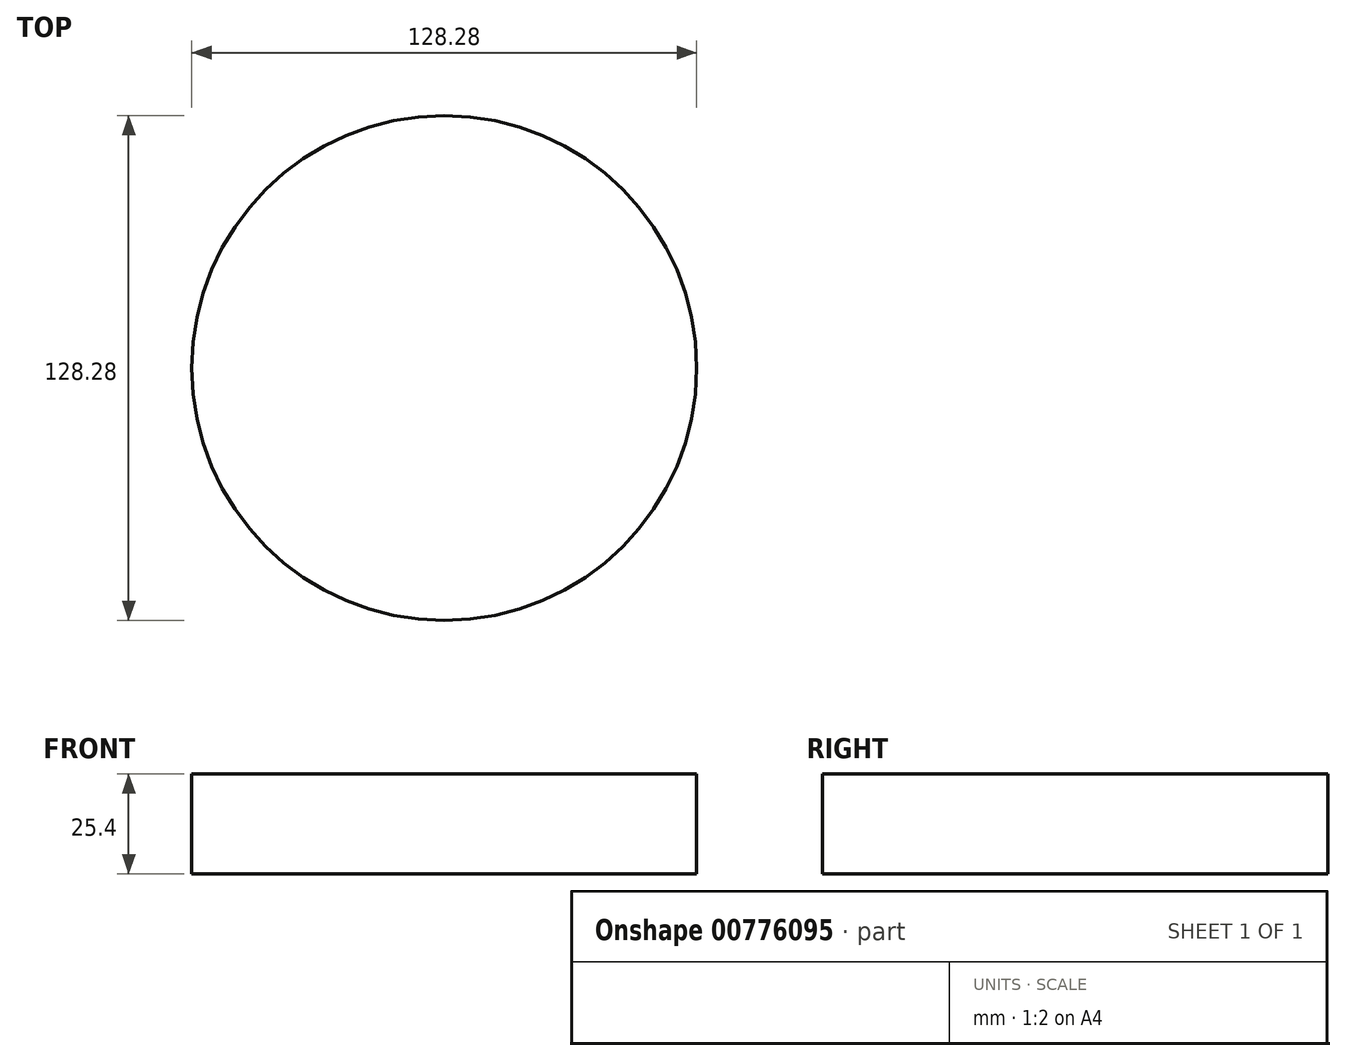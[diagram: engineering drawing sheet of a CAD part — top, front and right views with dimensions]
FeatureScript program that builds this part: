
annotation { "Feature Type Name" : "Feature", "Feature Type Description" : "" }
export const myFeature = defineFeature(function(context is Context, id is Id, definition is map)
    precondition{}
    {
        {
            var Q0;
            Q0=qCreatedBy(makeId("Top.planeOp"),FACE);
            var sketch = newSketch(context, id + "F0", { "sketchPlane" : qUnion([Q0])});
            skCircle(sketch, "E0", {"center": v(0, 0) * mm, "radius": 64.14 * mm});
            skSolve(sketch);
        }
        {
            var Q0;
            Q0=makeQuery(id+"F0.imprint","IMPRINT",FACE,{"disambiguationData":[TD([[makeQuery(id+"F0.imprint","IMPRINT",EDGE,{"derivedFrom":sQuery(id+"F0.wireOp",EDGE,"E0")}),1.0]])]});
            extrude(context, id + "F1", {"entities" : qUnion([Q0]), "depth" : 25.4 * mm, "offsetDistance" : 25.4 * mm});
        }
    });
